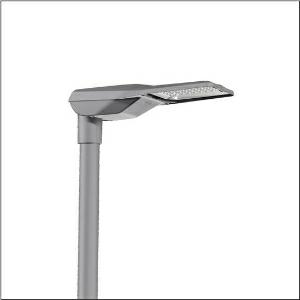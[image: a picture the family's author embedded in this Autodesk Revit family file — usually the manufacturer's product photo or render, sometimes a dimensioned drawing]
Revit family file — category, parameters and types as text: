
# Revit family: streetlight_sl_21_iq_mini___st1_0a_5xe2d31d08hb_45ae
name_source: partatom
category: Lighting Fixtures
units: mm (PartAtom-declared; Revit-internal decimal feet)

## family parameters
Cut with Voids When Loaded = No
Host = Face
Light Source = No
Part Type = Normal
Room Calculation Point = No
Round Connector Dimension = Use Diameter
Shared = No

## types (1)
- --- (1 x LED, 9450 lm, 70.9 W, 3000K)
    Apparent Load = 71 VA
    CIE Flux Codes = 37 72 97 100 100
    Color Rendering = 70
    Color Temperature = 3000K
    Default Elevation = 1800 mm
    Description = Streetlight SL 21 iQ mini, mast luminaire, primary light control with lens, of PMMA, primary optical cover: cover, of toughened safety glass, transparent, light distribution: ST1.0a, light emission: direct distribution, primary light characteristic: asymmetric, installation type: post-top, side-entry, LED, High Power LED, rated luminous flux: 9.450lm, luminous efficacy: 133lm/W, light colour: 730, colour temperature: 3000K, control gear: iQ-Comfort, control: Auto-Match, Temp-Guard, Lumen-Switch, Night-Set, Smart-Wire, Light-Fading, Desk-Remote (wireless, voltage-free reading and setting of iQ features in the workshop via application-optimized NFC function/RFID function), optimised constant luminous flux control (CLO 2.0), pre-setting: linear dimming characteristic, mains connection: 220..240V, AC, 50/60Hz, start of lifetime: 71W, end of service life: 75W, reduction: 31W, luminaire housing, of diecast aluminium, powder-coated, SITECO metallic grey (DB 702S), corrosivity category C5 high according to DIN EN ISO 12944, please order mast flange separately, inclination adjustable: 0°, 5°, 10°, 15°, sealing non-destructively replaceable, multi-level sealing system, length: 628mm, width: 235mm, height: 110mm, mast flange for spigot size: 42mm (side-entry): 5XC10008XM4, 60/48mm (side-entry/post-top): 5XC10108XM2, 76/60mm (side-entry/post-top): 5XC10108XM1, mounting height: 4..8m, protection rating (complete): IP66, insulation class (complete): insulation class II (safety insulation), certification: CE, ENEC, ENEC+, VDE, impact resistance: IK10, permissible operating ambient temperature for outdoor applications: -40..+50°C, standard-compliant lighting for roads and squares, packaging unit: 1 piece

Light Distribution: ST1.0a
    Height = 110 mm
    Lamp = 1 x LED
    Lamp Light Flux = 9450 lm
    Lamp Power = 70.9 W
    Lamp count = 1
    Length = 625 mm
    Luminous efficacy = 133 lm/W
    Manufacturer = Siteco
    ModVariant = No
    Model = 5XE2D31D08HB
    Number of Poles = 1
    OnlyDefault = Yes
    Power Factor = 1
    Product Name = Streetlight SL 21 iQ mini | ST1.0a
    Product group = mast luminaire | pylon top
    ProductGroupID = 6100
    Protection Class = Protection class II
    Protection Degree = IP 66
    RLX_Detail_Level = 1
    RLX_Emergency_Light_Flux = 0 lm
    RLX_Emergency_Type = 0
    RLX_Emergency_Type_DB = No
    RlxData = <blob elided: 26309 chars, md5=2dc0067b>
    Socket = socket
    Standby Power = 0 W
    System Light Flux = 9450 lm
    System Power = 71 W
    Type Comments = factory setting: luminous flux: 100 % | dim-lin: 254 | 711 mA
    Type Image = l_1003519.jpg
    URL = http://relux.com
    VarID = @adj_157641
    Voltage = 0 V
    Weight = 0.00 kg
    Width = 234 mm

## geometry (parser evidence)
native form markers: Blend x4, Sweep x12
no freeform markers — native parametric forms only
